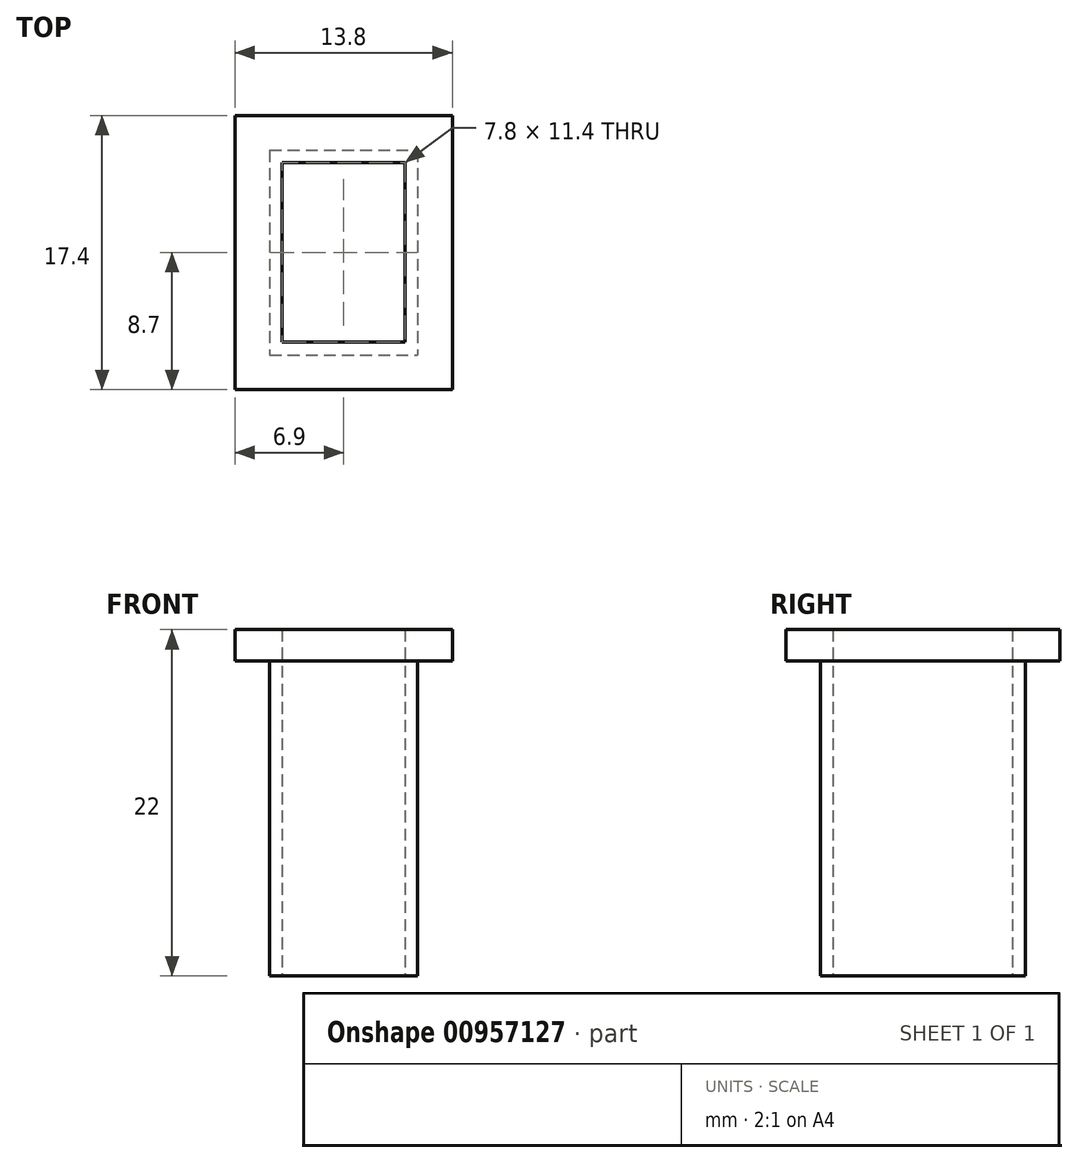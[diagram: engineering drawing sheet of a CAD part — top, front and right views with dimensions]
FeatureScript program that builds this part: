
annotation { "Feature Type Name" : "Feature", "Feature Type Description" : "" }
export const myFeature = defineFeature(function(context is Context, id is Id, definition is map)
    precondition{}
    {
        {
            var Q0;
            Q0=qCreatedBy(makeId("Top.planeOp"),FACE);
            var sketch = newSketch(context, id + "F0", { "sketchPlane" : qUnion([Q0])});
            skLineSegment(sketch, "E0.bottom", {"start": v(0, 0) * mm, "end": v(9.4, 0) * mm});
            skLineSegment(sketch, "E0.top", {"start": v(0, -13) * mm, "end": v(9.4, -13) * mm});
            skLineSegment(sketch, "E0.left", {"start": v(0, 0) * mm, "end": v(0, -13) * mm});
            skLineSegment(sketch, "E0.right", {"start": v(9.4, 0) * mm, "end": v(9.4, -13) * mm});
            skLineSegment(sketch, "E1.0", {"start": v(8.6, 0) * mm, "end": v(8.6, -13) * mm});
            skLineSegment(sketch, "E2.0", {"start": v(0, -12.2) * mm, "end": v(9.4, -12.2) * mm});
            skLineSegment(sketch, "E3.0", {"start": v(0.8, 0) * mm, "end": v(0.8, -13) * mm});
            skLineSegment(sketch, "E4.0", {"start": v(0, -0.8) * mm, "end": v(9.4, -0.8) * mm});
            skSolve(sketch);
        }
        {
            var Q0;
            {var subQ0=sQuery(id+"F0.wireOp",EDGE,"E0.left");var subQ1=sQuery(id+"F0.wireOp",EDGE,"E0.bottom");var subQ2=makeQuery(id+"F0.imprint","INTERSECT",VERTEX,{"derivedFrom":[subQ1,subQ0]});Q0=makeQuery(id+"F0.imprint","IMPRINT",FACE,{"disambiguationData":[TD([[makeQuery(id+"F0.imprint","IMPRINT",EDGE,{"disambiguationData":[TD([[subQ2,-1.0]])],"derivedFrom":subQ1}),-1.0]])]});}
            var Q1;
            {var subQ0=sQuery(id+"F0.wireOp",EDGE,"E2.0");var subQ1=sQuery(id+"F0.wireOp",EDGE,"E0.left");var subQ2=makeQuery(id+"F0.imprint","INTERSECT",VERTEX,{"derivedFrom":[subQ1,subQ0]});Q1=makeQuery(id+"F0.imprint","IMPRINT",FACE,{"disambiguationData":[TD([[makeQuery(id+"F0.imprint","IMPRINT",EDGE,{"disambiguationData":[TD([[subQ2,1.0]])],"derivedFrom":subQ1}),1.0]])]});}
            var Q2;
            {var subQ0=sQuery(id+"F0.wireOp",EDGE,"E0.left");var subQ1=sQuery(id+"F0.wireOp",EDGE,"E0.top");var subQ2=makeQuery(id+"F0.imprint","INTERSECT",VERTEX,{"derivedFrom":[subQ1,subQ0]});Q2=makeQuery(id+"F0.imprint","IMPRINT",FACE,{"disambiguationData":[TD([[makeQuery(id+"F0.imprint","IMPRINT",EDGE,{"disambiguationData":[TD([[subQ2,-1.0]])],"derivedFrom":subQ1}),1.0]])]});}
            var Q3;
            {var subQ0=sQuery(id+"F0.wireOp",EDGE,"E1.0");var subQ1=sQuery(id+"F0.wireOp",EDGE,"E0.top");var subQ2=makeQuery(id+"F0.imprint","INTERSECT",VERTEX,{"derivedFrom":[subQ1,subQ0]});Q3=makeQuery(id+"F0.imprint","IMPRINT",FACE,{"disambiguationData":[TD([[makeQuery(id+"F0.imprint","IMPRINT",EDGE,{"disambiguationData":[TD([[subQ2,1.0]])],"derivedFrom":subQ1}),1.0]])]});}
            var Q4;
            {var subQ0=sQuery(id+"F0.wireOp",EDGE,"E1.0");var subQ1=sQuery(id+"F0.wireOp",EDGE,"E0.bottom");var subQ2=makeQuery(id+"F0.imprint","INTERSECT",VERTEX,{"derivedFrom":[subQ1,subQ0]});Q4=makeQuery(id+"F0.imprint","IMPRINT",FACE,{"disambiguationData":[TD([[makeQuery(id+"F0.imprint","IMPRINT",EDGE,{"disambiguationData":[TD([[subQ2,1.0]])],"derivedFrom":subQ1}),-1.0]])]});}
            var Q5;
            {var subQ0=sQuery(id+"F0.wireOp",EDGE,"E0.right");var subQ1=sQuery(id+"F0.wireOp",EDGE,"E0.bottom");var subQ2=makeQuery(id+"F0.imprint","INTERSECT",VERTEX,{"derivedFrom":[subQ1,subQ0]});Q5=makeQuery(id+"F0.imprint","IMPRINT",FACE,{"disambiguationData":[TD([[makeQuery(id+"F0.imprint","IMPRINT",EDGE,{"disambiguationData":[TD([[subQ2,1.0]])],"derivedFrom":subQ1}),-1.0]])]});}
            var Q6;
            {var subQ0=sQuery(id+"F0.wireOp",EDGE,"E2.0");var subQ1=sQuery(id+"F0.wireOp",EDGE,"E0.right");var subQ2=makeQuery(id+"F0.imprint","INTERSECT",VERTEX,{"derivedFrom":[subQ1,subQ0]});Q6=makeQuery(id+"F0.imprint","IMPRINT",FACE,{"disambiguationData":[TD([[makeQuery(id+"F0.imprint","IMPRINT",EDGE,{"disambiguationData":[TD([[subQ2,1.0]])],"derivedFrom":subQ1}),-1.0]])]});}
            var Q7;
            {var subQ0=sQuery(id+"F0.wireOp",EDGE,"E0.right");var subQ1=sQuery(id+"F0.wireOp",EDGE,"E0.top");var subQ2=makeQuery(id+"F0.imprint","INTERSECT",VERTEX,{"derivedFrom":[subQ1,subQ0]});Q7=makeQuery(id+"F0.imprint","IMPRINT",FACE,{"disambiguationData":[TD([[makeQuery(id+"F0.imprint","IMPRINT",EDGE,{"disambiguationData":[TD([[subQ2,1.0]])],"derivedFrom":subQ1}),1.0]])]});}
            extrude(context, id + "F1", {"entities" : qUnion([Q0, Q1, Q2, Q3, Q4, Q5, Q6, Q7]), "depth" : 20 * mm, "offsetDistance" : 25 * mm});
        }
        {
            var Q0;
            Q0=makeQuery(id+"F1.opExtrude","CAP_FACE",FACE,{"disambiguationData":[OSD([sQuery(id+"F0.wireOp",EDGE,"E0.bottom"),sQuery(id+"F0.wireOp",EDGE,"E0.top"),sQuery(id+"F0.wireOp",EDGE,"E0.left"),sQuery(id+"F0.wireOp",EDGE,"E0.right"),sQuery(id+"F0.wireOp",EDGE,"E1.0"),sQuery(id+"F0.wireOp",EDGE,"E2.0"),sQuery(id+"F0.wireOp",EDGE,"E3.0"),sQuery(id+"F0.wireOp",EDGE,"E4.0")])],"isStart":false});
            var sketch = newSketch(context, id + "F2", { "sketchPlane" : qUnion([Q0])});
            skLineSegment(sketch, "E5.bottom", {"start": v(0.8, -0.8) * mm, "end": v(8.6, -0.8) * mm});
            skLineSegment(sketch, "E5.top", {"start": v(0.8, -12.2) * mm, "end": v(8.6, -12.2) * mm});
            skLineSegment(sketch, "E5.left", {"start": v(0.8, -0.8) * mm, "end": v(0.8, -12.2) * mm});
            skLineSegment(sketch, "E5.right", {"start": v(8.6, -0.8) * mm, "end": v(8.6, -12.2) * mm});
            skLineSegment(sketch, "E6.0", {"start": v(-2.2, 2.2) * mm, "end": v(-2.2, -15.2) * mm});
            skLineSegment(sketch, "E6.1", {"start": v(-2.2, 2.2) * mm, "end": v(11.6, 2.2) * mm});
            skLineSegment(sketch, "E6.2", {"start": v(11.6, 2.2) * mm, "end": v(11.6, -15.2) * mm});
            skLineSegment(sketch, "E6.3", {"start": v(-2.2, -15.2) * mm, "end": v(11.6, -15.2) * mm});
            skSolve(sketch);
        }
        {
            var Q0;
            Q0=makeQuery(id+"F2.imprint","IMPRINT",FACE,{"disambiguationData":[TD([[makeQuery(id+"F2.imprint","IMPRINT",EDGE,{"derivedFrom":sQuery(id+"F2.wireOp",EDGE,"E6.0")}),1.0]])]});
            var Q1;
            Q1=makeQuery(id+"F2.imprint","IMPRINT",FACE,{"disambiguationData":[TD([[makeQuery(id+"F2.imprint","IMPRINT",EDGE,{"derivedFrom":sQuery(id+"F2.wireOp",EDGE,"E5.bottom")}),1.0]])]});
            extrude(context, id + "F3", {"entities" : qUnion([Q0, Q1]), "operationType" : NewBodyOperationType.ADD, "depth" : 2 * mm, "offsetDistance" : 25 * mm});
        }
    });
